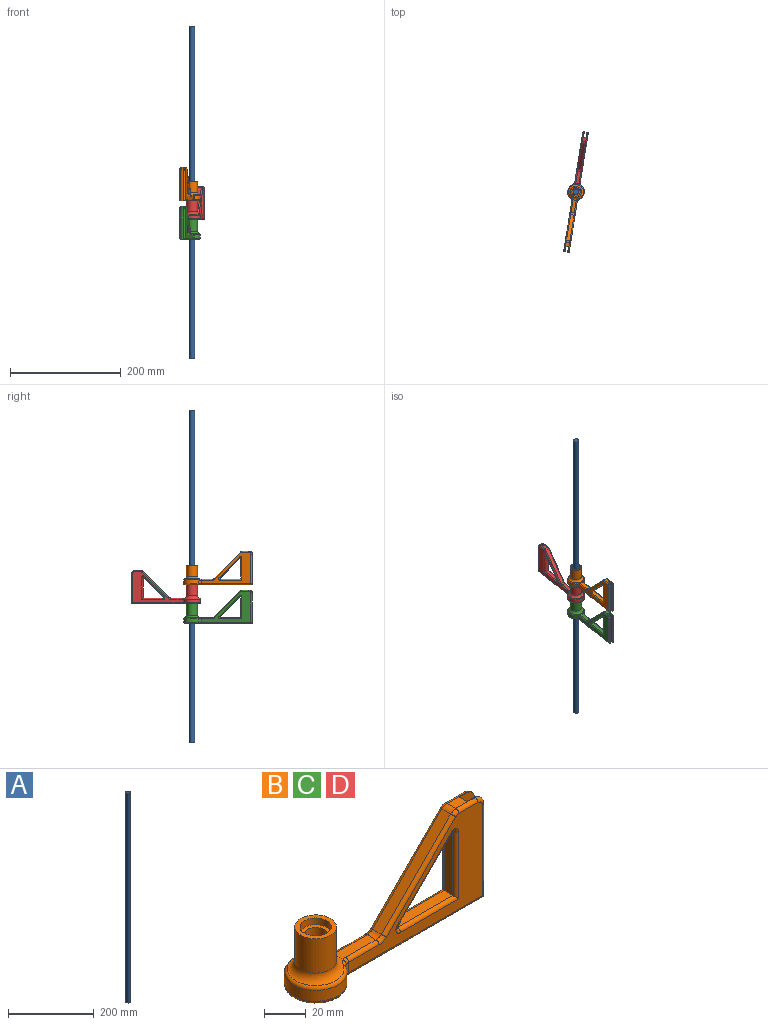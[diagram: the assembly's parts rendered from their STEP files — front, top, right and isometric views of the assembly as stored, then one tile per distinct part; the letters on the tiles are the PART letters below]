
ASSEMBLY  parts=4 mates=5
PART A: 3 faces, bbox 10x10x600 mm
  f0: cylinder r=5mm len=600mm, axis (0,0,-1), area 18849.6mm2, adj f1,f2
  f1: plane 10x10mm, normal (0,0,1), area 78.5mm2, adj f0
  f2: plane 10x10mm, normal (0,0,-1), area 78.5mm2, adj f0
PART B: 63 faces, bbox 130.5x40.2x60.4 mm
  f0: plane 55x0.5mm, normal (1,0,0), area 27.5mm2, adj f9,f18,f20,f35
  f1: cylinder r=5.25mm len=31mm, axis (0,0,-1), area 1022.6mm2, adj f9,f16
  f2: plane 37.59x6mm, normal (0,0,1), area 225.5mm2, adj f3,f28,f56,f60
  f3: plane 37.59x6mm, normal (-1,0,0), area 225.5mm2, adj f2,f27,f54,f58
  f4: plane 23.36x7.13mm, normal (0,0,1), area 139.1mm2, adj f21,f22,f46,f47,f48,f49
  f5: plane 90.68x56mm, normal (0,1,0), area 1577.4mm2, adj f25,f32,f34,f36,f38,f40,f42,f44
  f6: cylinder r=15mm len=30mm, axis (0,0,-1), area 494.2mm2, adj f25,f26,f29,f52
  f7: plane 90.68x56mm, normal (0,-1,0), area 1577.4mm2, adj f26,f33,f35,f37,f39,f41,f43,f45
  f8: plane 55x0.5mm, normal (1,0,0), area 27.5mm2, adj f9,f17,f23,f34
  f9: plane 123x26mm, normal (0,0,-1), area 983.8mm2, adj f0,f1,f8,f17,f18,f19,f29,f30
  f10: plane 12.93x6mm, normal (0,0,1), area 52.6mm2, adj f17,f18,f19,f20,f23,f24,f38,f39
  f11: plane 47.07x47.07mm, normal (-0.71,0,0.71), area 399.4mm2, adj f22,f24,f42,f43
  f12: plane 36.59x36.59mm, normal (0.71,0,-0.71), area 310.4mm2, adj f27,f28,f55,f61
  f13: cylinder r=10mm len=20mm, axis (0,0,-1), area 1256.6mm2, adj f14,f21
  f14: plane 20x20mm, normal (0,0,1), area 137.4mm2, adj f13,f15
  f15: cylinder r=7.5mm len=15mm, axis (0,0,1), area 188.5mm2, adj f14,f16
  f16: plane 15x15mm, normal (0,0,1), area 90.1mm2, adj f1,f15
  f17: plane 60x10mm, normal (0,-1,0), area 594.6mm2, adj f8,f9,f10,f19,f23
  f18: plane 60x10mm, normal (0,1,0), area 594.6mm2, adj f0,f9,f10,f19,f20
  f19: plane 60x5mm, normal (1,0,0), area 300mm2, adj f9,f10,f17,f18
  f20: cylinder r=5mm len=5mm, axis (0,-1,0), area 3.9mm2, adj f0,f10,f18,f37
  f21: torus R=15mm, axis (0,0,1), area 466.5mm2, adj f4,f13,f50,f51,f52
  f22: cylinder r=5mm len=6mm, axis (0,1,0), area 23.6mm2, adj f4,f11,f44,f45
  f23: cylinder r=5mm len=5mm, axis (0,-1,0), area 3.9mm2, adj f8,f10,f17,f36
  f24: cylinder r=5mm len=6mm, axis (0,-1,0), area 23.6mm2, adj f10,f11,f40,f41
  f25: cylinder r=5mm len=6.29mm, axis (0,0,-1), area 31.9mm2, adj f5,f6,f30,f48,f50
  f26: cylinder r=5mm len=6.29mm, axis (0,0,-1), area 31.9mm2, adj f6,f7,f31,f49,f51
  f27: cylinder r=1mm len=6mm, axis (0,-1,0), area 14.1mm2, adj f3,f12,f53,f59
  f28: cylinder r=1mm len=6mm, axis (0,1,0), area 14.1mm2, adj f2,f12,f57,f62
  f29: torus R=13mm, axis (0,0,1), area 234.8mm2, adj f6,f9,f30,f31
  f30: torus R=7mm, axis (0,0,1), area 18.8mm2, adj f9,f25,f29,f32
  f31: torus R=7mm, axis (0,0,1), area 18.8mm2, adj f9,f26,f29,f33
  f32: cylinder r=2mm len=92.68mm, axis (-1,0,0), area 288.9mm2, adj f5,f9,f30,f34
  f33: cylinder r=2mm len=92.68mm, axis (1,0,0), area 288.9mm2, adj f7,f9,f31,f35
  f34: cylinder r=2mm len=55mm, axis (0,0,-1), area 170.5mm2, adj f5,f8,f32,f36
  f35: cylinder r=2mm len=55mm, axis (0,0,-1), area 170.5mm2, adj f0,f7,f33,f37
  f36: torus R=3mm, axis (0,1,0), area 21.1mm2, adj f5,f23,f34,f38
  f37: torus R=3mm, axis (0,-1,0), area 21.1mm2, adj f7,f20,f35,f39
  f38: cylinder r=2mm len=12.93mm, axis (-1,0,0), area 40.6mm2, adj f5,f10,f36,f40
  f39: cylinder r=2mm len=12.93mm, axis (-1,0,0), area 40.6mm2, adj f7,f10,f37,f41
  f40: torus R=3mm, axis (0,1,0), area 10.5mm2, adj f5,f24,f38,f42
  f41: torus R=3mm, axis (0,-1,0), area 10.5mm2, adj f7,f24,f39,f43
  f42: cylinder r=2mm len=48.49mm, axis (-0.71,0,-0.71), area 209.1mm2, adj f5,f11,f40,f44
  f43: cylinder r=2mm len=48.49mm, axis (-0.71,0,-0.71), area 209.1mm2, adj f7,f11,f41,f45
  f44: torus R=7mm, axis (0,1,0), area 14.1mm2, adj f5,f22,f42,f46
  f45: torus R=7mm, axis (0,-1,0), area 14.1mm2, adj f7,f22,f43,f47
  f46: cylinder r=2mm len=20.61mm, axis (1,0,0), area 64.7mm2, adj f4,f5,f44,f48
  f47: cylinder r=2mm len=20.61mm, axis (-1,0,0), area 64.7mm2, adj f4,f7,f45,f49
  f48: torus R=7mm, axis (0,0,1), area 7.3mm2, adj f4,f25,f46,f50
  f49: torus R=7mm, axis (0,0,1), area 7.3mm2, adj f4,f26,f47,f51
  f50: bspline ~4.74x4.68mm, area 10mm2, adj f21,f25,f48,f52
  f51: bspline ~4.74x4.68mm, area 10mm2, adj f21,f26,f49,f52
  f52: torus R=13mm, axis (0,0,-1), area 194.5mm2, adj f6,f21,f50,f51
  f53: torus R=3mm, axis (0,1,0), area 12.8mm2, adj f5,f27,f54,f55
  f54: cylinder r=2mm len=39.59mm, axis (0,0,-1), area 120.4mm2, adj f3,f5,f53,f56
  f55: cylinder r=2mm len=38mm, axis (0.71,0,0.71), area 162.5mm2, adj f5,f12,f53,f57
  f56: cylinder r=2mm len=39.59mm, axis (1,0,0), area 120.4mm2, adj f2,f5,f54,f57
  f57: torus R=3mm, axis (0,1,0), area 12.8mm2, adj f5,f28,f55,f56
  f58: cylinder r=2mm len=39.59mm, axis (0,0,-1), area 120.4mm2, adj f3,f7,f59,f60
  f59: torus R=3mm, axis (0,-1,0), area 12.8mm2, adj f7,f27,f58,f61
  f60: cylinder r=2mm len=39.59mm, axis (-1,0,0), area 120.4mm2, adj f2,f7,f58,f62
  f61: cylinder r=2mm len=38mm, axis (0.71,0,0.71), area 162.5mm2, adj f7,f12,f59,f62
  f62: torus R=3mm, axis (0,-1,0), area 12.8mm2, adj f7,f28,f60,f61
PART C: same geometry as B
PART D: same geometry as B
PLACE A rot(axis=(1,0,0),0deg) t=(0,0,0)mm
PLACE B rot(axis=(0,0,-1),99.1deg) t=(0,0,284.5)mm
PLACE C rot(axis=(0,0,-1),99.1deg) t=(0,0,214.5)mm
PLACE D rot(axis=(0,0,1),80.9deg) t=(0,0,249.5)mm
MATE revolute A.f0 <-> B.f1  axis (0,0,-1) through (0,0,300)mm
MATE parallel C.f5 <-> B.f5  axis (0.99,-0.16,0) through (-12.18,-107.43,243)mm
MATE revolute C.f1 <-> A.f0  axis (0,0,-1) through (0,0,230)mm
MATE parallel B.f5 <-> D.f7  axis (0.99,-0.16,0) through (-9.64,-91.63,332.09)mm
MATE revolute D.f1 <-> A.f0  axis (0,0,-1) through (0,0,265)mm
